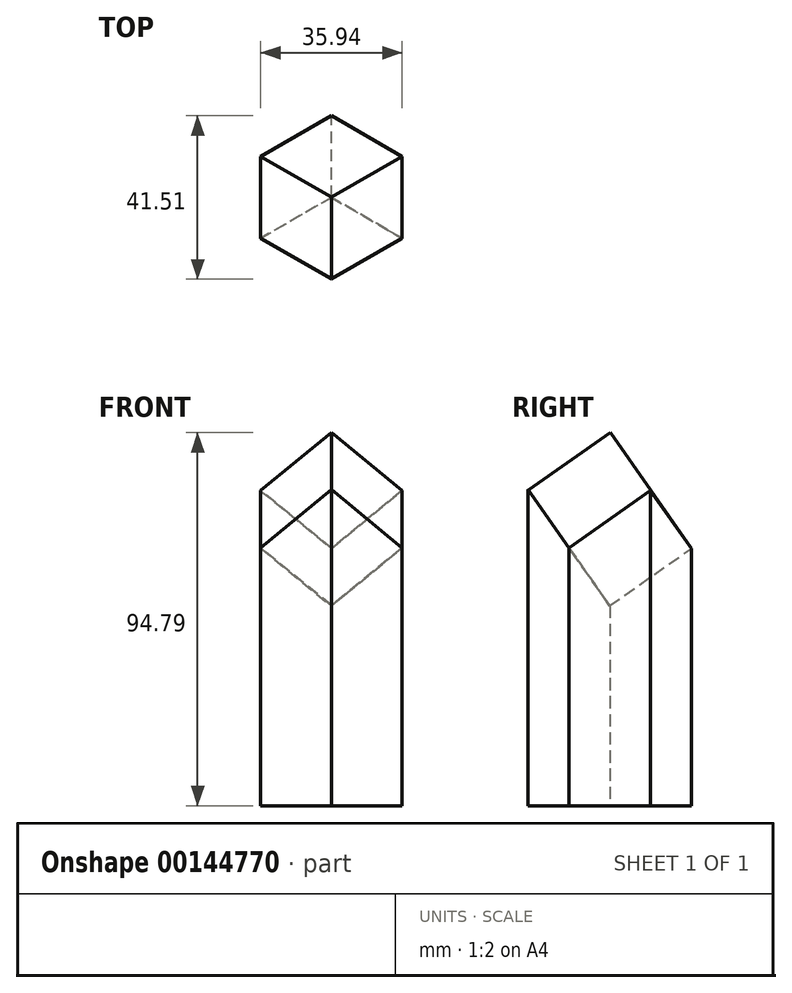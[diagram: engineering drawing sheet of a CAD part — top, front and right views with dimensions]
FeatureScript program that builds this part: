
annotation { "Feature Type Name" : "Feature", "Feature Type Description" : "" }
export const myFeature = defineFeature(function(context is Context, id is Id, definition is map)
    precondition{}
    {
        {
            var Q0;
            Q0=qCreatedBy(makeId("Top.planeOp"),FACE);
            var sketch = newSketch(context, id + "F0", { "sketchPlane" : qUnion([Q0])});
            skLineSegment(sketch, "E0.bottom", {"start": v(12.7, -12.7) * mm, "end": v(-12.7, -12.7) * mm});
            skLineSegment(sketch, "E0.top", {"start": v(12.7, 12.7) * mm, "end": v(-12.7, 12.7) * mm});
            skLineSegment(sketch, "E0.left", {"start": v(12.7, -12.7) * mm, "end": v(12.7, 12.7) * mm});
            skLineSegment(sketch, "E0.right", {"start": v(-12.7, -12.7) * mm, "end": v(-12.7, 12.7) * mm});
            skPoint(sketch, "E0.middle", {"position": v(0, 0) * mm});
            skSolve(sketch);
        }
        {
            var Q0;
            Q0=makeQuery(id+"F0.imprint","IMPRINT",FACE,{"disambiguationData":[TD([[makeQuery(id+"F0.imprint","IMPRINT",EDGE,{"derivedFrom":sQuery(id+"F0.wireOp",EDGE,"E0.bottom")}),-1.0]])]});
            extrude(context, id + "F1", {"entities" : qUnion([Q0]), "depth" : 76.2 * mm, "hasSecondDirection" : true, "secondDirectionOppositeDirection" : false, "secondDirectionDepth" : 50.8 * mm});
        }
        {
            var Q0;
            Q0=makeQuery(id+"F1.opExtrude","SWEPT_BODY",BODY,{"disambiguationData":[OSD([sQuery(id+"F0.wireOp",EDGE,"E0.bottom"),sQuery(id+"F0.wireOp",EDGE,"E0.top"),sQuery(id+"F0.wireOp",EDGE,"E0.left"),sQuery(id+"F0.wireOp",EDGE,"E0.right")])]});
            var Q1;
            Q1=makeQuery(id+"F1.opExtrude","CAP_EDGE",EDGE,{"disambiguationData":[OSD([sQuery(id+"F0.wireOp",EDGE,"E0.left")])],"isStart":true});
            transform(context, id + "F2", {"entities" : qUnion([Q0]), "transformType" : TransformType.ROTATION, "transformAxis" : qUnion([Q1]), "angle" : 45 * degree, "makeCopy" : false});
        }
        {
            var Q0;
            Q0=makeQuery(id+"F1.opExtrude","SWEPT_FACE",FACE,{"disambiguationData":[OSD([sQuery(id+"F0.wireOp",EDGE,"E0.bottom")])]});
            var sketch = newSketch(context, id + "F3", { "sketchPlane" : qUnion([Q0])});
            skLineSegment(sketch, "E1", {"start": v(12.7, 50.8) * mm, "end": v(34.46, 50.8) * mm});
            skSolve(sketch);
        }
        {
            var Q0;
            Q0=makeQuery(id+"F1.opExtrude","SWEPT_BODY",BODY,{"disambiguationData":[OSD([sQuery(id+"F0.wireOp",EDGE,"E0.bottom"),sQuery(id+"F0.wireOp",EDGE,"E0.top"),sQuery(id+"F0.wireOp",EDGE,"E0.left"),sQuery(id+"F0.wireOp",EDGE,"E0.right")])]});
            var Q1;
            Q1=sQuery(id+"F3.wireOp",EDGE,"E1");
            transform(context, id + "F4", {"entities" : qUnion([Q0]), "transformType" : TransformType.ROTATION, "transformAxis" : qUnion([Q1]), "angle" : 35 * degree, "makeCopy" : false});
        }
        {
            var Q0;
            Q0=qCreatedBy(makeId("Top.planeOp"),FACE);
            var sketch = newSketch(context, id + "F5", { "sketchPlane" : qUnion([Q0])});
            skCircle(sketch, "E2.cCircle", {"center": v(12.7, -12.65) * mm, "radius": 17.97 * mm, "construction": true});
            skLineSegment(sketch, "E2.0", {"start": v(30.67, -2.27) * mm, "end": v(30.67, -23.02) * mm});
            skLineSegment(sketch, "E2.1", {"start": v(30.67, -23.02) * mm, "end": v(12.7, -33.4) * mm});
            skLineSegment(sketch, "E2.2", {"start": v(12.7, -33.4) * mm, "end": v(-5.27, -23.02) * mm});
            skLineSegment(sketch, "E2.3", {"start": v(-5.27, -23.02) * mm, "end": v(-5.27, -2.27) * mm});
            skLineSegment(sketch, "E2.4", {"start": v(-5.27, -2.27) * mm, "end": v(12.7, 8.1) * mm});
            skLineSegment(sketch, "E2.5", {"start": v(12.7, 8.1) * mm, "end": v(30.67, -2.27) * mm});
            skPoint(sketch, "E2.0.midPoint", {"position": v(30.67, -12.65) * mm});
            skLineSegment(sketch, "E3", {"start": v(12.7, -12.65) * mm, "end": v(30.67, -23.02) * mm});
            skLineSegment(sketch, "E4", {"start": v(12.7, -12.65) * mm, "end": v(12.7, 8.1) * mm});
            skLineSegment(sketch, "E5", {"start": v(12.7, -12.65) * mm, "end": v(-5.27, -23.02) * mm});
            skSolve(sketch);
        }
        {
            var Q0;
            Q0=makeQuery(id+"F5.imprint","IMPRINT",FACE,{"disambiguationData":[TD([[makeQuery(id+"F5.imprint","IMPRINT",EDGE,{"derivedFrom":sQuery(id+"F5.wireOp",EDGE,"E2.0")}),-1.0]])]});
            var Q1;
            Q1=makeQuery(id+"F1.opExtrude","SWEPT_FACE",FACE,{"disambiguationData":[OSD([sQuery(id+"F0.wireOp",EDGE,"E0.left")])]});
            extrude(context, id + "F6", {"entities" : qUnion([Q0]), "operationType" : NewBodyOperationType.ADD, "endBound" : BoundingType.UP_TO_SURFACE, "endBoundEntityFace" : qUnion([Q1]), "depth" : 25.4 * mm});
        }
        {
            var Q0;
            Q0=makeQuery(id+"F5.imprint","IMPRINT",FACE,{"disambiguationData":[TD([[makeQuery(id+"F5.imprint","IMPRINT",EDGE,{"derivedFrom":sQuery(id+"F5.wireOp",EDGE,"E2.1")}),-1.0]])]});
            var Q1;
            Q1=makeQuery(id+"F1.opExtrude","SWEPT_FACE",FACE,{"disambiguationData":[OSD([sQuery(id+"F0.wireOp",EDGE,"E0.bottom")])]});
            extrude(context, id + "F7", {"entities" : qUnion([Q0]), "endBound" : BoundingType.UP_TO_SURFACE, "endBoundEntityFace" : qUnion([Q1]), "depth" : 25.4 * mm});
        }
        {
            var Q0;
            Q0=makeQuery(id+"F5.imprint","IMPRINT",FACE,{"disambiguationData":[TD([[makeQuery(id+"F5.imprint","IMPRINT",EDGE,{"derivedFrom":sQuery(id+"F5.wireOp",EDGE,"E2.3")}),-1.0]])]});
            var Q1;
            Q1=makeQuery(id+"F1.opExtrude","CAP_FACE",FACE,{"disambiguationData":[OSD([sQuery(id+"F0.wireOp",EDGE,"E0.bottom"),sQuery(id+"F0.wireOp",EDGE,"E0.top"),sQuery(id+"F0.wireOp",EDGE,"E0.left"),sQuery(id+"F0.wireOp",EDGE,"E0.right")])],"isStart":true});
            extrude(context, id + "F8", {"entities" : qUnion([Q0]), "endBound" : BoundingType.UP_TO_SURFACE, "endBoundEntityFace" : qUnion([Q1]), "depth" : 25.4 * mm});
        }
    });
